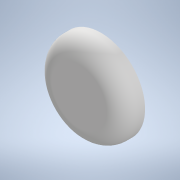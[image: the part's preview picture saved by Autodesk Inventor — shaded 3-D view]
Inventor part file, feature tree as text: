
AUTODESK INVENTOR PART (.ipt)
format: ipt  version: 2020.2 (Build 242310000, 310)  size: 120,320 bytes
history: native  units: in
note: dims shown in document units (in); Inventor stores cm internally (conversion verified against a paired STEP export)
features: revolve x1, fillet x1, sketch x1
ambient origin geometry x8: Origin, YZ Plane, XZ Plane, XY Plane, X Axis, Y Axis, Z Axis, Center Point
bodies: Solid1 (feature_tree)
feature tree (3):
  revolve  "Revolution1"  [1 undecoded]
  fillet  "Fillet1"  [1 undecoded]
  sketch  "Sketch1"  dims[d0=1.5748in d1=0.7874in d2=90.0deg d3=0.5906in]
note: 2 required parameter values undecoded (feature->parameter linkage not recoverable at this tier; creation-order binding heuristic only, values carry confidence <= 0.55)